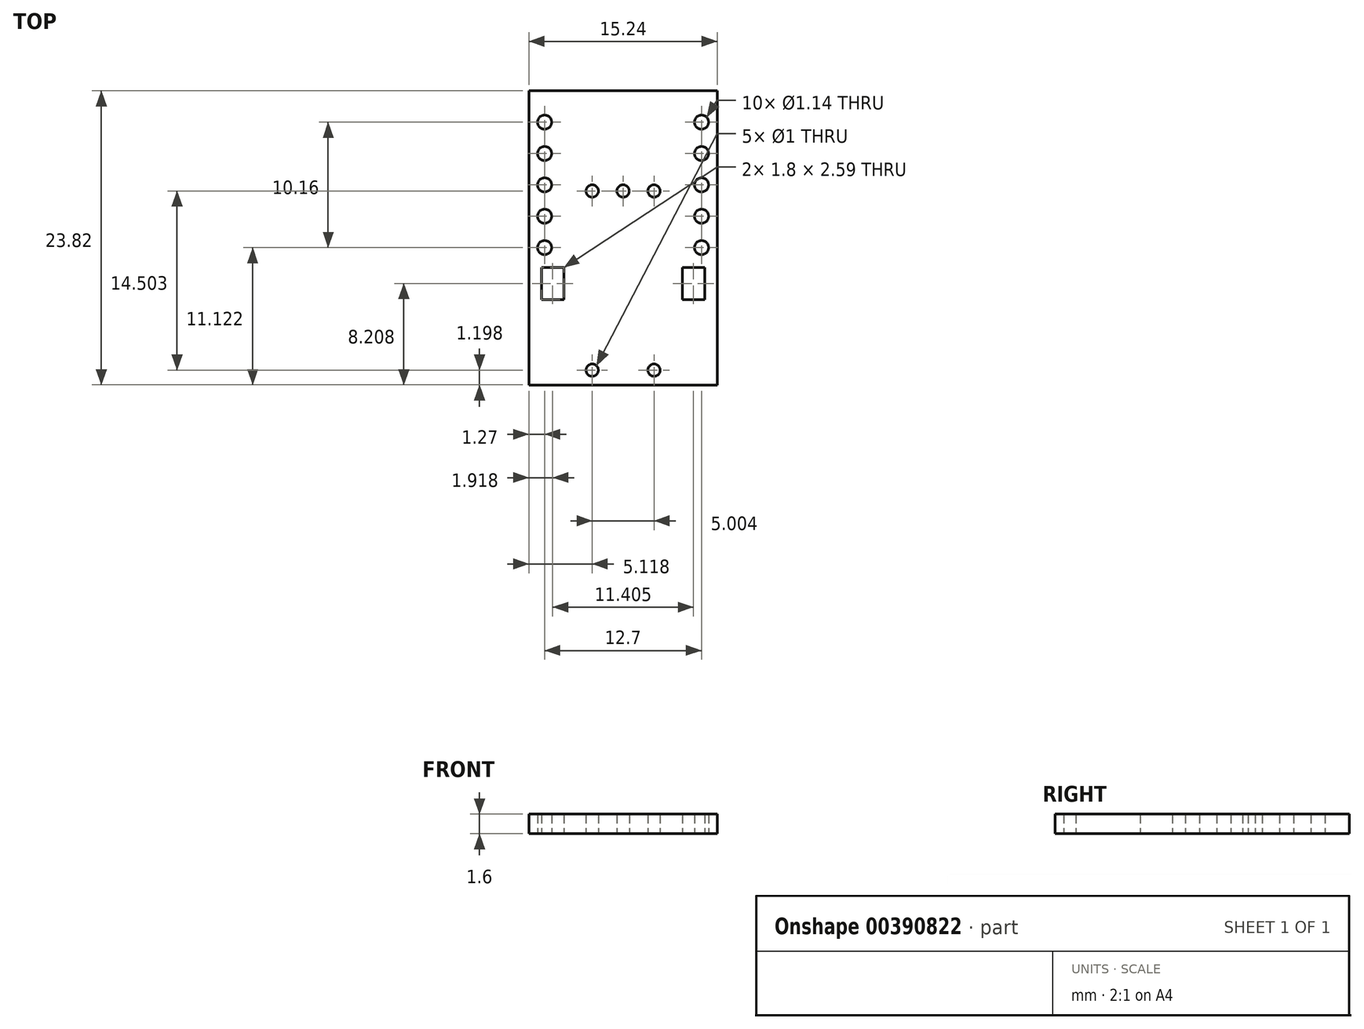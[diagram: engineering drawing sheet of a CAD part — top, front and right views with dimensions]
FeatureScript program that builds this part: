
annotation { "Feature Type Name" : "Feature", "Feature Type Description" : "" }
export const myFeature = defineFeature(function(context is Context, id is Id, definition is map)
    precondition{}
    {
        {
            var Q0;
            Q0=qCreatedBy(makeId("Top.planeOp"),FACE);
            var sketch = newSketch(context, id + "F0", { "sketchPlane" : qUnion([Q0])});
            skLineSegment(sketch, "E0.bottom", {"start": v(-7.62, 11.91) * mm, "end": v(7.62, 11.91) * mm});
            skLineSegment(sketch, "E0.top", {"start": v(-7.62, -11.91) * mm, "end": v(7.62, -11.91) * mm});
            skLineSegment(sketch, "E0.left", {"start": v(-7.62, 11.91) * mm, "end": v(-7.62, -11.91) * mm});
            skLineSegment(sketch, "E0.right", {"start": v(7.62, 11.91) * mm, "end": v(7.62, -11.91) * mm});
            skPoint(sketch, "E0.middle", {"position": v(0, 0) * mm});
            skCircle(sketch, "E1", {"center": v(6.35, -0.79) * mm, "radius": 0.57 * mm});
            skCircle(sketch, "E2.1.0.0", {"center": v(6.35, 1.75) * mm, "radius": 0.57 * mm});
            skCircle(sketch, "E2.2.0.0", {"center": v(6.35, 4.3) * mm, "radius": 0.57 * mm});
            skCircle(sketch, "E2.3.0.0", {"center": v(6.35, 6.83) * mm, "radius": 0.57 * mm});
            skCircle(sketch, "E2.4.0.0", {"center": v(6.35, 9.37) * mm, "radius": 0.57 * mm});
            skLineSegment(sketch, "E2.direction1", {"start": v(6.35, -0.79) * mm, "end": v(6.35, 1.75) * mm, "construction": true});
            skLineSegment(sketch, "E3", {"start": v(0, 22.9) * mm, "end": v(0, -49.1) * mm, "construction": true});
            skCircle(sketch, "E4.MirrorC", {"center": v(-6.35, -0.79) * mm, "radius": 0.57 * mm});
            skCircle(sketch, "E5.MirrorC", {"center": v(-6.35, 1.75) * mm, "radius": 0.57 * mm});
            skCircle(sketch, "E6.MirrorC", {"center": v(-6.35, 4.3) * mm, "radius": 0.57 * mm});
            skCircle(sketch, "E7.MirrorC", {"center": v(-6.35, 9.37) * mm, "radius": 0.57 * mm});
            skCircle(sketch, "E8.MirrorC", {"center": v(-6.35, 6.83) * mm, "radius": 0.57 * mm});
            skSolve(sketch);
        }
        {
            var Q0;
            Q0=qSketchRegion(id+"F0",true);
            extrude(context, id + "F1", {"entities" : qUnion([Q0]), "depth" : 1.6 * mm});
        }
        {
            var Q0;
            Q0=qCreatedBy(makeId("Top.planeOp"),FACE);
            var sketch = newSketch(context, id + "F2", { "sketchPlane" : qUnion([Q0])});
            skCircle(sketch, "E9", {"center": v(2.5, -10.71) * mm, "radius": 0.5 * mm});
            skCircle(sketch, "E10", {"center": v(0, 3.8) * mm, "radius": 0.5 * mm});
            skCircle(sketch, "E11", {"center": v(-2.5, 3.8) * mm, "radius": 0.5 * mm});
            skCircle(sketch, "E12", {"center": v(-2.5, -10.71) * mm, "radius": 0.5 * mm});
            skCircle(sketch, "E13", {"center": v(2.5, 3.8) * mm, "radius": 0.5 * mm});
            skLineSegment(sketch, "E14", {"start": v(0, -3.7) * mm, "end": v(0, -10.12) * mm, "construction": true});
            skLineSegment(sketch, "E15.bottom", {"start": v(-4.8, -5) * mm, "end": v(-6.6, -5) * mm});
            skLineSegment(sketch, "E15.top", {"start": v(-4.8, -2.4) * mm, "end": v(-6.6, -2.4) * mm});
            skLineSegment(sketch, "E15.left", {"start": v(-4.8, -5) * mm, "end": v(-4.8, -2.4) * mm});
            skLineSegment(sketch, "E15.right", {"start": v(-6.6, -5) * mm, "end": v(-6.6, -2.4) * mm});
            skPoint(sketch, "E15.middle", {"position": v(-5.7, -3.7) * mm});
            skLineSegment(sketch, "E16.MirrorCS", {"start": v(4.8, -5) * mm, "end": v(4.8, -2.4) * mm});
            skLineSegment(sketch, "E17.MirrorCS", {"start": v(4.8, -5) * mm, "end": v(6.6, -5) * mm});
            skLineSegment(sketch, "E18.MirrorCS", {"start": v(6.6, -5) * mm, "end": v(6.6, -2.4) * mm});
            skLineSegment(sketch, "E19.MirrorCS", {"start": v(4.8, -2.4) * mm, "end": v(6.6, -2.4) * mm});
            skSolve(sketch);
        }
        {
            var Q0;
            Q0 = qSketchRegion(id + "F2", true);
            extrude(context, id + "F3", {"entities" : qUnion([Q0]), "operationType" : NewBodyOperationType.REMOVE, "endBound" : BoundingType.THROUGH_ALL, "depth" : 25.4 * mm});
        }
    });
